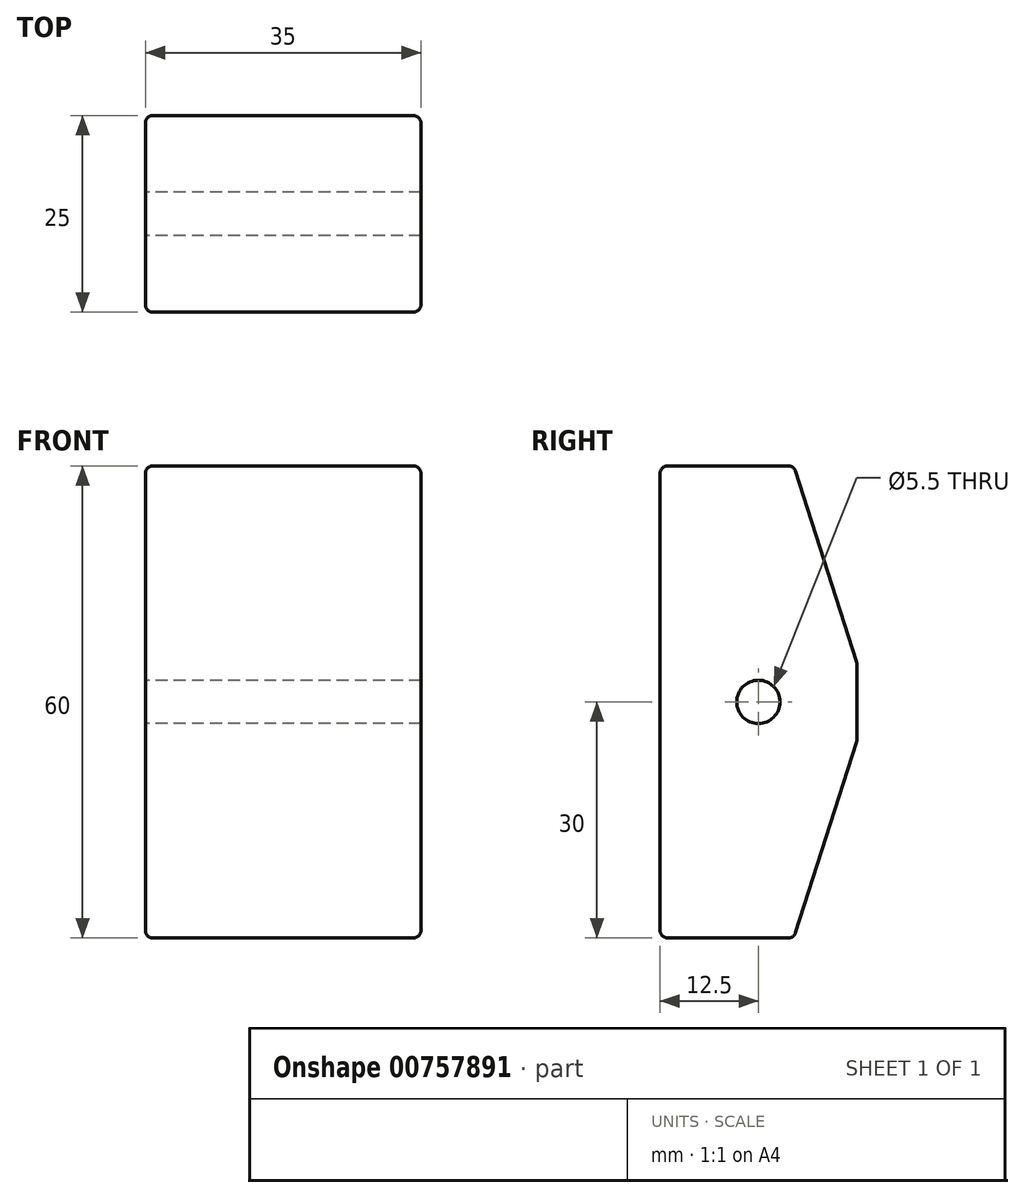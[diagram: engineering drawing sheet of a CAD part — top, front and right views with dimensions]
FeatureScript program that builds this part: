
annotation { "Feature Type Name" : "Feature", "Feature Type Description" : "" }
export const myFeature = defineFeature(function(context is Context, id is Id, definition is map)
    precondition{}
    {
        {
            var Q0;
            Q0=qCreatedBy(makeId("Top.planeOp"),FACE);
            var sketch = newSketch(context, id + "F0", { "sketchPlane" : qUnion([Q0])});
            skLineSegment(sketch, "E0.bottom", {"start": v(17.5, -12.5) * mm, "end": v(-17.5, -12.5) * mm});
            skLineSegment(sketch, "E0.top", {"start": v(17.5, 12.5) * mm, "end": v(-17.5, 12.5) * mm});
            skLineSegment(sketch, "E0.left", {"start": v(17.5, -12.5) * mm, "end": v(17.5, 12.5) * mm});
            skLineSegment(sketch, "E0.right", {"start": v(-17.5, -12.5) * mm, "end": v(-17.5, 12.5) * mm});
            skPoint(sketch, "E0.middle", {"position": v(0, 0) * mm});
            skSolve(sketch);
        }
        {
            var Q0;
            Q0=makeQuery(id+"F0.imprint","IMPRINT",FACE,{"disambiguationData":[TD([[makeQuery(id+"F0.imprint","IMPRINT",EDGE,{"derivedFrom":sQuery(id+"F0.wireOp",EDGE,"E0.bottom")}),-1.0]])]});
            extrude(context, id + "F1", {"entities" : qUnion([Q0]), "depth" : 60 * mm, "offsetDistance" : 25 * mm});
        }
        {
            var Q0;
            Q0=makeQuery(id+"F1.opExtrude","SWEPT_FACE",FACE,{"disambiguationData":[OSD([sQuery(id+"F0.wireOp",EDGE,"E0.left")])]});
            var sketch = newSketch(context, id + "F2", { "sketchPlane" : qUnion([Q0])});
            skPoint(sketch, "E1", {"position": v(0, 30) * mm});
            skSolve(sketch);
        }
        {
            var Q0;
            Q0=sQuery(id+"F2.wireOp",VERTEX,"E1");
            var Q1;
            Q1=makeQuery(id+"F1.opExtrude","SWEPT_BODY",BODY,{"disambiguationData":[OSD([sQuery(id+"F0.wireOp",EDGE,"E0.bottom"),sQuery(id+"F0.wireOp",EDGE,"E0.top"),sQuery(id+"F0.wireOp",EDGE,"E0.left"),sQuery(id+"F0.wireOp",EDGE,"E0.right")])]});
            hole(context, id + "F3", {"style" : HoleStyle.SIMPLE, "endStyle" : HoleEndStyle.BLIND, "holeDiameter" : 5.5 * mm, "majorDiameter" : 5 * mm, "holeDepth" : 35 * mm, "isTappedThrough" : true, "tappedDepth" : 12 * mm, "tapClearance" : 3, "startFromSketch" : true, "locations" : qUnion([Q0]), "scope" : qUnion([Q1])});
        }
        {
            var Q0;
            Q0=makeQuery(id+"F1.opExtrude","CAP_EDGE",EDGE,{"disambiguationData":[OSD([sQuery(id+"F0.wireOp",EDGE,"E0.top")])],"isStart":false});
            var Q1;
            Q1=makeQuery(id+"F1.opExtrude","CAP_EDGE",EDGE,{"disambiguationData":[OSD([sQuery(id+"F0.wireOp",EDGE,"E0.top")])],"isStart":true});
            chamfer(context, id + "F4", {"entities" : qUnion([Q0, Q1]), "chamferType" : ChamferType.TWO_OFFSETS, "width1" : 8 * mm, "oppositeDirection" : false, "width2" : 25 * mm, "tangentPropagation" : true});
        }
        {
            var Q0;
            {var subQ0=sQuery(id+"F0.wireOp",EDGE,"E0.top");Q0=makeQuery(id+"F4.opChamfer","BLEND_FACE",FACE,{"disambiguationData":[OSD([subQ0]),TDD([makeQuery(id+"F1.opExtrude","CAP_EDGE",EDGE,{"disambiguationData":[OSD([subQ0])],"isStart":false})])]});}
            var Q1;
            Q1=makeQuery(id+"F1.opExtrude","SWEPT_FACE",FACE,{"disambiguationData":[OSD([sQuery(id+"F0.wireOp",EDGE,"E0.top")])]});
            var Q2;
            {var subQ0=sQuery(id+"F0.wireOp",EDGE,"E0.top");Q2=makeQuery(id+"F4.opChamfer","BLEND_FACE",FACE,{"disambiguationData":[OSD([subQ0]),TDD([makeQuery(id+"F1.opExtrude","CAP_EDGE",EDGE,{"disambiguationData":[OSD([subQ0])],"isStart":true})])]});}
            var Q3;
            Q3=makeQuery(id+"F1.opExtrude","CAP_FACE",FACE,{"disambiguationData":[OSD([sQuery(id+"F0.wireOp",EDGE,"E0.bottom"),sQuery(id+"F0.wireOp",EDGE,"E0.top"),sQuery(id+"F0.wireOp",EDGE,"E0.left"),sQuery(id+"F0.wireOp",EDGE,"E0.right")])],"isStart":false});
            var Q4;
            Q4=makeQuery(id+"F1.opExtrude","SWEPT_FACE",FACE,{"disambiguationData":[OSD([sQuery(id+"F0.wireOp",EDGE,"E0.bottom")])]});
            var Q5;
            Q5=makeQuery(id+"F1.opExtrude","CAP_FACE",FACE,{"disambiguationData":[OSD([sQuery(id+"F0.wireOp",EDGE,"E0.bottom"),sQuery(id+"F0.wireOp",EDGE,"E0.top"),sQuery(id+"F0.wireOp",EDGE,"E0.left"),sQuery(id+"F0.wireOp",EDGE,"E0.right")])],"isStart":true});
            fillet(context, id + "F5", {"entities" : qUnion([Q0, Q1, Q2, Q3, Q4, Q5]), "tangentPropagation" : true, "radius" : 1 * mm, "defaultsChanged" : false, "isVariable" : true, "vertexSettings" : [], "smoothTransition" : false, "allowEdgeOverflow" : false});
        }
    });
